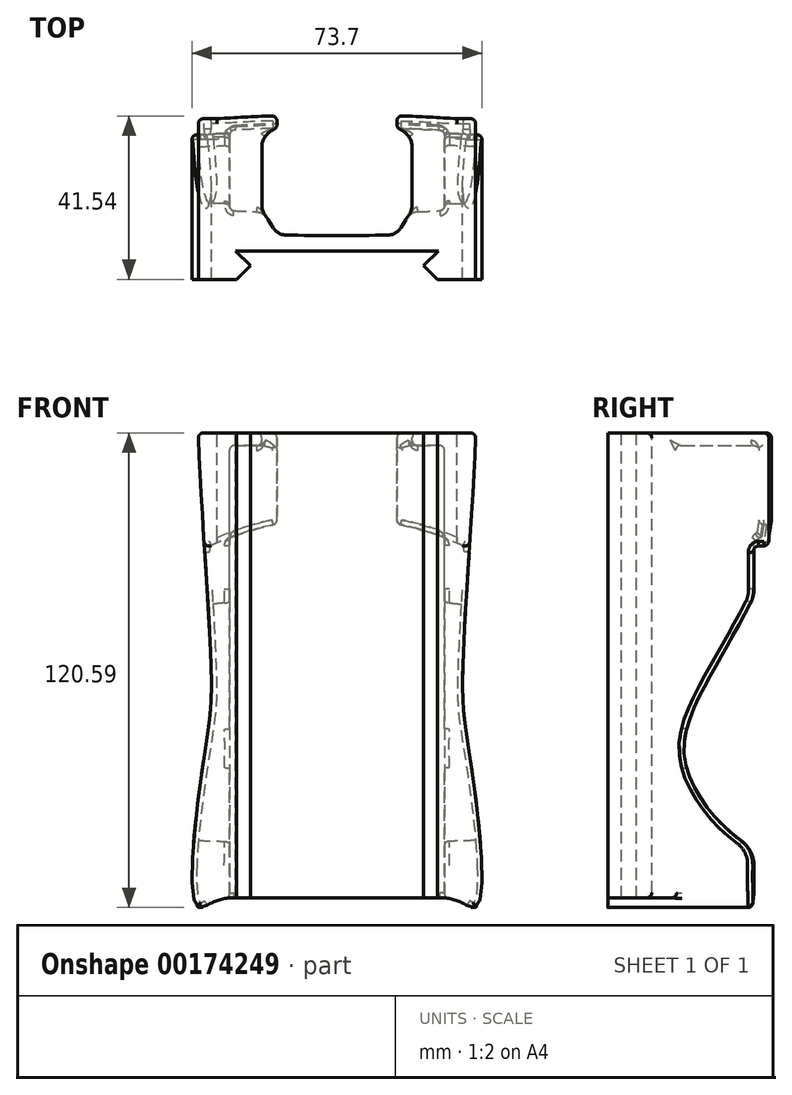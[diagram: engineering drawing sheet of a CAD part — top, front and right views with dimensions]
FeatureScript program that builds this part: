
annotation { "Feature Type Name" : "Feature", "Feature Type Description" : "" }
export const myFeature = defineFeature(function(context is Context, id is Id, definition is map)
    precondition{}
    {
        {
            var Q0;
            Q0=qCreatedBy(makeId("Top.planeOp"),FACE);
            var sketch = newSketch(context, id + "F0", { "sketchPlane" : qUnion([Q0])});
            skLineSegment(sketch, "E0", {"start": v(30.48, -10.36) * mm, "end": v(30.48, 30.47) * mm});
            skLineSegment(sketch, "E1", {"start": v(27.3, 27.49) * mm, "end": v(27.3, 7.17) * mm});
            skArc(sketch, "E2", {"start": v(20.63, 6.82) * mm, "mid": v(23.97, 6.98) * mm, "end": v(27.3, 7.17) * mm});
            skArc(sketch, "E3", {"start": v(0, 0.76) * mm, "mid": v(6.56, 0.8) * mm, "end": v(13.12, 0.95) * mm});
            skLineSegment(sketch, "E4", {"start": v(16.3, 2.85) * mm, "end": v(17.5, 4.91) * mm});
            skPoint(sketch, "E5.orphan", {"position": v(15.25, 1.01) * mm});
            skPoint(sketch, "E6.visualSharp", {"position": v(18.55, 6.73) * mm});
            skArc(sketch, "E6.filletArc", {"start": v(20.63, 6.82) * mm, "mid": v(18.82, 6.27) * mm, "end": v(17.5, 4.91) * mm});
            skArc(sketch, "E7.filletArc", {"start": v(13.12, 0.95) * mm, "mid": v(14.96, 1.48) * mm, "end": v(16.3, 2.85) * mm});
            skLineSegment(sketch, "E8", {"start": v(0, 0) * mm, "end": v(0, -3.13) * mm});
            skArc(sketch, "E9", {"start": v(27.3, 27.49) * mm, "mid": v(21.28, 27.8) * mm, "end": v(15.25, 28.05) * mm});
            skArc(sketch, "E10", {"start": v(30.48, 30.47) * mm, "mid": v(22.87, 30.9) * mm, "end": v(15.25, 31.22) * mm});
            skPoint(sketch, "E11.start.orphan", {"position": v(30.48, 27.99) * mm});
            skLineSegment(sketch, "E12.trimOffspring", {"start": v(0, 0.76) * mm, "end": v(0, -3.13) * mm});
            skLineSegment(sketch, "E13", {"start": v(15.25, 31.22) * mm, "end": v(15.25, 28.05) * mm});
            skLineSegment(sketch, "E14", {"start": v(0, -3.13) * mm, "end": v(25.78, -3.13) * mm});
            skLineSegment(sketch, "E15", {"start": v(25.78, -3.13) * mm, "end": v(22.02, -6.89) * mm});
            skLineSegment(sketch, "E16", {"start": v(0, -6.89) * mm, "end": v(29.89, -6.89) * mm, "construction": true});
            skLineSegment(sketch, "E17", {"start": v(25.5, -10.36) * mm, "end": v(30.48, -10.36) * mm});
            skLineSegment(sketch, "E18", {"start": v(22.02, -6.89) * mm, "end": v(25.5, -10.36) * mm});
            skSolve(sketch);
        }
        {
            var Q0;
            Q0 = qSketchRegion(id + "F0", true);
            extrude(context, id + "F1", {"entities" : qUnion([Q0]), "oppositeDirection" : true, "depth" : 118.11 * mm});
        }
        {
            var Q0;
            Q0=makeQuery(id+"F1.opExtrude","SWEPT_FACE",FACE,{"disambiguationData":[OSD([sQuery(id+"F0.wireOp",EDGE,"E17")])]});
            var sketch = newSketch(context, id + "F2", { "sketchPlane" : qUnion([Q0])});
            skLineSegment(sketch, "E19", {"start": v(30.48, 0) * mm, "end": v(35.28, 0) * mm});
            skFitSpline(sketch, "E20", {"points": [v(30.48, -118.11) * mm, v(35.61, -120.17) * mm, v(33.76, -82.17) * mm, v(31.9, -64.6) * mm, v(33.93, -25.26) * mm, v(35.28, 0) * mm], "startDerivative": vector(61.38, -50.25) * mm, "endDerivative": vector(5.05, 107.66) * mm});
            skLineSegment(sketch, "E21", {"start": v(30.48, -118.11) * mm, "end": v(30.48, 0) * mm});
            skSolve(sketch);
        }
        {
            var Q0;
            Q0 = qSketchRegion(id + "F2", true);
            var Q1;
            Q1=makeQuery(id+"F1.opExtrude","SWEPT_FACE",FACE,{"disambiguationData":[OSD([sQuery(id+"F0.wireOp",EDGE,"E10")])]});
            extrude(context, id + "F3", {"entities" : qUnion([Q0]), "operationType" : NewBodyOperationType.ADD, "oppositeDirection" : true, "endBoundEntityFace" : qUnion([Q1]), "depth" : 40.84 * mm});
        }
        {
            var Q0;
            Q0=makeQuery(id+"F1.opExtrude","CAP_VERTEX",VERTEX,{"disambiguationData":[OSD([sQuery(id+"F0.wireOp",EDGE,"E0"),sQuery(id+"F0.wireOp",EDGE,"E10")])],"isStart":false});
            var Q1;
            Q1=makeQuery(id+"F1.opExtrude","CAP_VERTEX",VERTEX,{"disambiguationData":[OSD([sQuery(id+"F0.wireOp",EDGE,"E0"),sQuery(id+"F0.wireOp",EDGE,"E10")])],"isStart":true});
            var Q2;
            Q2=makeQuery(id+"F1.opExtrude","CAP_VERTEX",VERTEX,{"disambiguationData":[OSD([sQuery(id+"F0.wireOp",EDGE,"E10"),sQuery(id+"F0.wireOp",EDGE,"MdokXZck-MeQf-Ru8W-Up0K-fHNruu8GMaJc")])],"isStart":true});
            cPlane(context, id + "F4", {"entities" : qUnion([Q0, Q1, Q2]), "cplaneType" : CPlaneType.THREE_POINT, "offset" : 50.8 * mm, "oppositeDirection" : true, "width" : 152.4 * mm, "height" : 152.4 * mm});
        }
        {
            var Q0;
            Q0=qCreatedBy(id+"F4.planeOp",FACE);
            var sketch = newSketch(context, id + "F5", { "sketchPlane" : qUnion([Q0])});
            skLineSegment(sketch, "E22", {"start": v(1.4, 0) * mm, "end": v(1.4, -106.44) * mm, "construction": true});
            skCircle(sketch, "E23", {"center": v(1.4, -97.8) * mm, "radius": 76.2 * mm});
            skSolve(sketch);
        }
        {
            var Q0;
            Q0 = qSketchRegion(id + "F5", true);
            extrude(context, id + "F6", {"entities" : qUnion([Q0]), "operationType" : NewBodyOperationType.REMOVE, "oppositeDirection" : true, "depth" : 3.8 * mm, "hasSecondDirection" : true, "secondDirectionBound" : SecondDirectionBoundingType.THROUGH_ALL, "secondDirectionOppositeDirection" : false, "secondDirectionDepth" : 25.4 * mm});
        }
        {
            var Q0;
            Q0=qCreatedBy(makeId("Top.planeOp"),FACE);
            var sketch = newSketch(context, id + "F7", { "sketchPlane" : qUnion([Q0])});
            skLineSegment(sketch, "E24", {"start": v(19.1, 29.35) * mm, "end": v(27.88, 29.04) * mm});
            skLineSegment(sketch, "E25", {"start": v(27.88, 29.04) * mm, "end": v(27.88, 0) * mm});
            skLineSegment(sketch, "E26", {"start": v(27.88, 0) * mm, "end": v(19.1, 0) * mm});
            skLineSegment(sketch, "E27", {"start": v(19.1, 0) * mm, "end": v(19.1, 29.35) * mm});
            skPoint(sketch, "E28.orphan", {"position": v(0, 30.02) * mm});
            skSolve(sketch);
        }
        {
            var Q0;
            Q0 = qSketchRegion(id + "F7", true);
            extrude(context, id + "F8", {"entities" : qUnion([Q0]), "operationType" : NewBodyOperationType.ADD, "oppositeDirection" : true, "depth" : 3.17 * mm});
        }
        {
            var Q0;
            Q0=makeQuery(id+"F1.opExtrude","SWEPT_FACE",FACE,{"disambiguationData":[OSD([sQuery(id+"F0.wireOp",EDGE,"E1")])]});
            var sketch = newSketch(context, id + "F9", { "sketchPlane" : qUnion([Q0])});
            skLineSegment(sketch, "E29", {"start": v(-29.4, -36.02) * mm, "end": v(-29.4, -107.37) * mm});
            skFitSpline(sketch, "E30", {"points": [v(-29.4, -36.02) * mm, v(-14.24, -64.34) * mm, v(-9.36, -84.1) * mm, v(-29.4, -107.37) * mm], "startDerivative": vector(39.36, -85.52) * mm, "endDerivative": vector(-85.37, -44.58) * mm});
            skSolve(sketch);
        }
        {
            var Q0;
            {var subQ0=sQuery(id+"F9.wireOp",EDGE,"E30");var subQ1=makeQuery(id+"F6.boolean.opBoolean","INTERSECT",EDGE,{"derivedFrom":[makeQuery(id+"F1.opExtrude","SWEPT_FACE",FACE,{"disambiguationData":[OSD([sQuery(id+"F0.wireOp",EDGE,"E1")])]}),makeQuery(id+"F6.opExtrude","CAP_FACE",FACE,{"disambiguationData":[OSD([sQuery(id+"F5.wireOp",EDGE,"E23")])],"isStart":false})]});var subQ2=makeQuery(id+"F9.imprint","INTERSECT",VERTEX,{"disambiguationData":[OD(0.0)],"derivedFrom":[subQ1,subQ0]});Q0=makeQuery(id+"F9.imprint","IMPRINT",FACE,{"disambiguationData":[TD([[makeQuery(id+"F9.imprint","IMPRINT",EDGE,{"disambiguationData":[TD([[subQ2,-1.0]])],"derivedFrom":subQ0}),-1.0]])]});}
            extrude(context, id + "F10", {"entities" : qUnion([Q0]), "operationType" : NewBodyOperationType.REMOVE, "endBound" : BoundingType.THROUGH_ALL, "oppositeDirection" : true, "depth" : 25.4 * mm});
        }
        {
            var Q0;
            Q0=makeQuery(id+"F10.boolean.opBoolean","INTERSECT",EDGE,{"disambiguationData":[OD(1.0)],"derivedFrom":[makeQuery(id+"F6.boolean.opBoolean","COPY",FACE,{"derivedFrom":makeQuery(id+"F6.opExtrude","CAP_FACE",FACE,{"disambiguationData":[OSD([sQuery(id+"F5.wireOp",EDGE,"E23")])],"isStart":false})}),makeQuery(id+"F10.opExtrude","SWEPT_FACE",FACE,{"disambiguationData":[OSD([sQuery(id+"F9.wireOp",EDGE,"E30")])]})]});
            var Q1;
            Q1=makeQuery(id+"F10.boolean.opBoolean","INTERSECT",EDGE,{"disambiguationData":[OD(0.0)],"derivedFrom":[makeQuery(id+"F6.boolean.opBoolean","COPY",FACE,{"derivedFrom":makeQuery(id+"F6.opExtrude","CAP_FACE",FACE,{"disambiguationData":[OSD([sQuery(id+"F5.wireOp",EDGE,"E23")])],"isStart":false})}),makeQuery(id+"F10.opExtrude","SWEPT_FACE",FACE,{"disambiguationData":[OSD([sQuery(id+"F9.wireOp",EDGE,"E30")])]})]});
            fillet(context, id + "F11", {"entities" : qUnion([Q0, Q1]), "radius" : 7.62 * mm, "tangentPropagation" : true, "allowEdgeOverflow" : false});
        }
        {
            var Q0;
            Q0=makeQuery(id+"F8.boolean.opBoolean","INTERSECT",EDGE,{"derivedFrom":[makeQuery(id+"F1.opExtrude","SWEPT_FACE",FACE,{"disambiguationData":[OSD([sQuery(id+"F0.wireOp",EDGE,"E9")])]}),makeQuery(id+"F8.opExtrude","SWEPT_FACE",FACE,{"disambiguationData":[OSD([sQuery(id+"F7.wireOp",EDGE,"E27")])]})]});
            fillet(context, id + "F12", {"entities" : qUnion([Q0]), "radius" : 5.08 * mm, "tangentPropagation" : true, "allowEdgeOverflow" : false});
        }
        {
            var Q0;
            Q0=makeQuery(id+"F8.boolean.opBoolean","INTERSECT",EDGE,{"derivedFrom":[makeQuery(id+"F1.opExtrude","SWEPT_FACE",FACE,{"disambiguationData":[OSD([sQuery(id+"F0.wireOp",EDGE,"E6.filletArc")])]}),makeQuery(id+"F8.opExtrude","SWEPT_FACE",FACE,{"disambiguationData":[OSD([sQuery(id+"F7.wireOp",EDGE,"E27")])]})]});
            fillet(context, id + "F13", {"entities" : qUnion([Q0]), "radius" : 5.08 * mm, "tangentPropagation" : true, "allowEdgeOverflow" : false});
        }
        {
            var Q0;
            Q0=makeQuery(id+"F3.boolean.opBoolean","MERGE",EDGE,{"derivedFrom":[makeQuery(id+"F1.opExtrude","CAP_EDGE",EDGE,{"disambiguationData":[OSD([sQuery(id+"F0.wireOp",EDGE,"E0")])],"isStart":false}),makeQuery(id+"F3.opExtrude","SWEPT_EDGE",EDGE,{"disambiguationData":[OSD([sQuery(id+"F0.wireOp",EDGE,"E17"),sQuery(id+"F2.wireOp",EDGE,"E20"),sQuery(id+"F2.wireOp",EDGE,"E21")])]})]});
            fillet(context, id + "F14", {"entities" : qUnion([Q0]), "radius" : 12.7 * mm, "tangentPropagation" : true, "allowEdgeOverflow" : false});
        }
        {
            var Q0;
            Q0=makeQuery(id+"F10.boolean.opBoolean","INTERSECT",EDGE,{"derivedFrom":[makeQuery(id+"F3.opExtrude","SWEPT_FACE",FACE,{"disambiguationData":[OSD([sQuery(id+"F2.wireOp",EDGE,"E20")])]}),makeQuery(id+"F10.opExtrude","SWEPT_FACE",FACE,{"disambiguationData":[OSD([sQuery(id+"F9.wireOp",EDGE,"E30")])]})]});
            var Q1;
            Q1=makeQuery(id+"F10.boolean.opBoolean","COPY",EDGE,{"derivedFrom":makeQuery(id+"F10.opExtrude","CAP_EDGE",EDGE,{"disambiguationData":[OSD([sQuery(id+"F9.wireOp",EDGE,"E30")])],"isStart":true})});
            fillet(context, id + "F15", {"entities" : qUnion([Q0, Q1]), "radius" : 1.27 * mm, "tangentPropagation" : true, "allowEdgeOverflow" : false});
        }
        {
            var Q0;
            Q0=makeQuery(id+"F6.boolean.opBoolean","INTERSECT",EDGE,{"derivedFrom":[makeQuery(id+"F1.opExtrude","SWEPT_FACE",FACE,{"disambiguationData":[OSD([sQuery(id+"F0.wireOp",EDGE,"E10")])]}),makeQuery(id+"F6.opExtrude","SWEPT_FACE",FACE,{"disambiguationData":[OSD([sQuery(id+"F5.wireOp",EDGE,"E23")])]})]});
            fillet(context, id + "F16", {"entities" : qUnion([Q0]), "radius" : 1.27 * mm, "tangentPropagation" : true, "allowEdgeOverflow" : false});
        }
        {
            var Q0;
            Q0=makeQuery(id+"F1.opExtrude","SWEPT_EDGE",EDGE,{"disambiguationData":[OSD([sQuery(id+"F0.wireOp",EDGE,"E1"),sQuery(id+"F0.wireOp",EDGE,"E2")])]});
            var Q1;
            Q1=makeQuery(id+"F8.boolean.opBoolean","INTERSECT",EDGE,{"derivedFrom":[makeQuery(id+"F1.opExtrude","SWEPT_FACE",FACE,{"disambiguationData":[OSD([sQuery(id+"F0.wireOp",EDGE,"E1")])]}),makeQuery(id+"F8.opExtrude","CAP_FACE",FACE,{"disambiguationData":[OSD([sQuery(id+"F7.wireOp",EDGE,"E24"),sQuery(id+"F7.wireOp",EDGE,"E25"),sQuery(id+"F7.wireOp",EDGE,"E26"),sQuery(id+"F7.wireOp",EDGE,"E27")])],"isStart":false})]});
            var Q2;
            Q2=makeQuery(id+"F1.opExtrude","SWEPT_EDGE",EDGE,{"disambiguationData":[OSD([sQuery(id+"F0.wireOp",EDGE,"E1"),sQuery(id+"F0.wireOp",EDGE,"E9")])]});
            var Q3;
            Q3=makeQuery(id+"F8.boolean.opBoolean","INTERSECT",EDGE,{"derivedFrom":[makeQuery(id+"F1.opExtrude","SWEPT_FACE",FACE,{"disambiguationData":[OSD([sQuery(id+"F0.wireOp",EDGE,"E9")])]}),makeQuery(id+"F8.opExtrude","CAP_FACE",FACE,{"disambiguationData":[OSD([sQuery(id+"F7.wireOp",EDGE,"E24"),sQuery(id+"F7.wireOp",EDGE,"E25"),sQuery(id+"F7.wireOp",EDGE,"E26"),sQuery(id+"F7.wireOp",EDGE,"E27")])],"isStart":false})]});
            fillet(context, id + "F17", {"entities" : qUnion([Q0, Q1, Q2, Q3]), "radius" : 1.27 * mm, "tangentPropagation" : true, "allowEdgeOverflow" : false});
        }
        {
            var Q0;
            Q0=makeQuery(id+"F6.boolean.opBoolean","INTERSECT",EDGE,{"derivedFrom":[makeQuery(id+"F1.opExtrude","SWEPT_FACE",FACE,{"disambiguationData":[OSD([sQuery(id+"F0.wireOp",EDGE,"E9")])]}),makeQuery(id+"F6.opExtrude","SWEPT_FACE",FACE,{"disambiguationData":[OSD([sQuery(id+"F5.wireOp",EDGE,"E23")])]})]});
            fillet(context, id + "F18", {"entities" : qUnion([Q0]), "radius" : 1.27 * mm, "tangentPropagation" : true, "allowEdgeOverflow" : false});
        }
        {
            var Q0;
            Q0=makeQuery(id+"F6.boolean.opBoolean","COPY",EDGE,{"derivedFrom":makeQuery(id+"F6.opExtrude","CAP_EDGE",EDGE,{"disambiguationData":[OSD([sQuery(id+"F5.wireOp",EDGE,"E23")])],"isStart":false})});
            fillet(context, id + "F19", {"entities" : qUnion([Q0]), "radius" : 1.27 * mm, "tangentPropagation" : true, "allowEdgeOverflow" : false});
        }
        {
            var Q0;
            Q0=makeQuery(id+"F6.boolean.opBoolean","INTERSECT",EDGE,{"derivedFrom":[makeQuery(id+"F3.opExtrude","CAP_FACE",FACE,{"disambiguationData":[OSD([sQuery(id+"F2.wireOp",EDGE,"E19"),sQuery(id+"F2.wireOp",EDGE,"E20"),sQuery(id+"F2.wireOp",EDGE,"E21")])],"isStart":false}),makeQuery(id+"F6.opExtrude","SWEPT_FACE",FACE,{"disambiguationData":[OSD([sQuery(id+"F5.wireOp",EDGE,"E23")])]})]});
            fillet(context, id + "F20", {"entities" : qUnion([Q0]), "radius" : 1.27 * mm, "tangentPropagation" : true, "allowEdgeOverflow" : false});
        }
        {
            var Q0;
            Q0=makeQuery(id+"F3.opExtrude","CAP_EDGE",EDGE,{"disambiguationData":[OSD([sQuery(id+"F2.wireOp",EDGE,"E20")])],"isStart":false});
            fillet(context, id + "F21", {"entities" : qUnion([Q0]), "radius" : 1.27 * mm, "tangentPropagation" : true, "allowEdgeOverflow" : false});
        }
        {
            var Q0;
            Q0=makeQuery(id+"F8.boolean.opBoolean","INTERSECT",EDGE,{"derivedFrom":[makeQuery(id+"F1.opExtrude","SWEPT_FACE",FACE,{"disambiguationData":[OSD([sQuery(id+"F0.wireOp",EDGE,"E2")])]}),makeQuery(id+"F8.opExtrude","CAP_FACE",FACE,{"disambiguationData":[OSD([sQuery(id+"F7.wireOp",EDGE,"E24"),sQuery(id+"F7.wireOp",EDGE,"E25"),sQuery(id+"F7.wireOp",EDGE,"E26"),sQuery(id+"F7.wireOp",EDGE,"E27")])],"isStart":false})]});
            var Q1;
            Q1=makeQuery(id+"F8.opExtrude","CAP_EDGE",EDGE,{"disambiguationData":[OSD([sQuery(id+"F7.wireOp",EDGE,"E27")])],"isStart":false});
            var Q2;
            Q2=makeQuery(id+"F8.opExtrude","CAP_EDGE",EDGE,{"disambiguationData":[OSD([sQuery(id+"F7.wireOp",EDGE,"E27")])],"isStart":true});
            var Q3;
            Q3=makeQuery(id+"F1.opExtrude","SWEPT_EDGE",EDGE,{"disambiguationData":[OSD([sQuery(id+"F0.wireOp",EDGE,"E9"),sQuery(id+"F0.wireOp",EDGE,"E13")])]});
            var Q4;
            Q4=makeQuery(id+"F1.opExtrude","CAP_EDGE",EDGE,{"disambiguationData":[OSD([sQuery(id+"F0.wireOp",EDGE,"E10")])],"isStart":true});
            var Q5;
            Q5=makeQuery(id+"F1.opExtrude","CAP_EDGE",EDGE,{"disambiguationData":[OSD([sQuery(id+"F0.wireOp",EDGE,"E13")])],"isStart":true});
            fillet(context, id + "F22", {"entities" : qUnion([Q0, Q1, Q2, Q3, Q4, Q5]), "radius" : 1.27 * mm, "tangentPropagation" : true, "allowEdgeOverflow" : false});
        }
        {
            var Q0;
            Q0=makeQuery(id+"F12.opFillet","BLEND_EDGE",EDGE,{"blendedFrom":[makeQuery(id+"F8.boolean.opBoolean","INTERSECT",EDGE,{"derivedFrom":[makeQuery(id+"F1.opExtrude","SWEPT_FACE",FACE,{"disambiguationData":[OSD([sQuery(id+"F0.wireOp",EDGE,"E9")])]}),makeQuery(id+"F8.opExtrude","SWEPT_FACE",FACE,{"disambiguationData":[OSD([sQuery(id+"F7.wireOp",EDGE,"E27")])]})]}),makeQuery(id+"F1.opExtrude","SWEPT_FACE",FACE,{"disambiguationData":[OSD([sQuery(id+"F0.wireOp",EDGE,"E13")])]})],"blendedInto":[makeQuery(id+"F1.opExtrude","SWEPT_FACE",FACE,{"disambiguationData":[OSD([sQuery(id+"F0.wireOp",EDGE,"E13")])]})]});
            fillet(context, id + "F23", {"entities" : qUnion([Q0]), "radius" : 1.27 * mm, "tangentPropagation" : true, "allowEdgeOverflow" : false});
        }
        {
            var Q0;
            Q0=makeQuery(id+"F3.opExtrude","SWEPT_EDGE",EDGE,{"disambiguationData":[OSD([sQuery(id+"F2.wireOp",EDGE,"E19"),sQuery(id+"F2.wireOp",EDGE,"E20")])]});
            fillet(context, id + "F24", {"entities" : qUnion([Q0]), "radius" : 1.27 * mm, "tangentPropagation" : true, "allowEdgeOverflow" : false});
        }
        {
            var Q0;
            Q0=makeQuery(id+"F1.opExtrude","CAP_EDGE",EDGE,{"disambiguationData":[OSD([sQuery(id+"F0.wireOp",EDGE,"E3")])],"isStart":false});
            fillet(context, id + "F25", {"entities" : qUnion([Q0]), "radius" : 1.27 * mm, "tangentPropagation" : true, "allowEdgeOverflow" : false});
        }
        {
            var Q0;
            Q0=makeQuery(id+"F1.opExtrude","SWEPT_BODY",BODY,{"disambiguationData":[OSD([sQuery(id+"F0.wireOp",EDGE,"2er3J34T-UetY-1yPx-DaCZ-OkgeTg1K8kIv"),sQuery(id+"F0.wireOp",EDGE,"E0"),sQuery(id+"F0.wireOp",EDGE,"E1"),sQuery(id+"F0.wireOp",EDGE,"E2"),sQuery(id+"F0.wireOp",EDGE,"E3"),sQuery(id+"F0.wireOp",EDGE,"E4"),sQuery(id+"F0.wireOp",EDGE,"E6.filletArc"),sQuery(id+"F0.wireOp",EDGE,"E7.filletArc"),sQuery(id+"F0.wireOp",EDGE,"tuMWJgsS-k7Jv-nQoi-J3SB-pvlRjHGqRAIn"),sQuery(id+"F0.wireOp",EDGE,"hivBriIb-3i2S-iEXT-tcMf-GkjieWFGtZ04"),sQuery(id+"F0.wireOp",EDGE,"E9"),sQuery(id+"F0.wireOp",EDGE,"E10"),sQuery(id+"F0.wireOp",EDGE,"E12.trimOffspring"),sQuery(id+"F0.wireOp",EDGE,"E13")])]});
            var Q1;
            Q1=qCreatedBy(makeId("Right.planeOp"),FACE);
            mirror(context, id + "F26", {"operationType" : NewBodyOperationType.ADD, "entities" : qUnion([Q0]), "mirrorPlane" : qUnion([Q1])});
        }
    });
